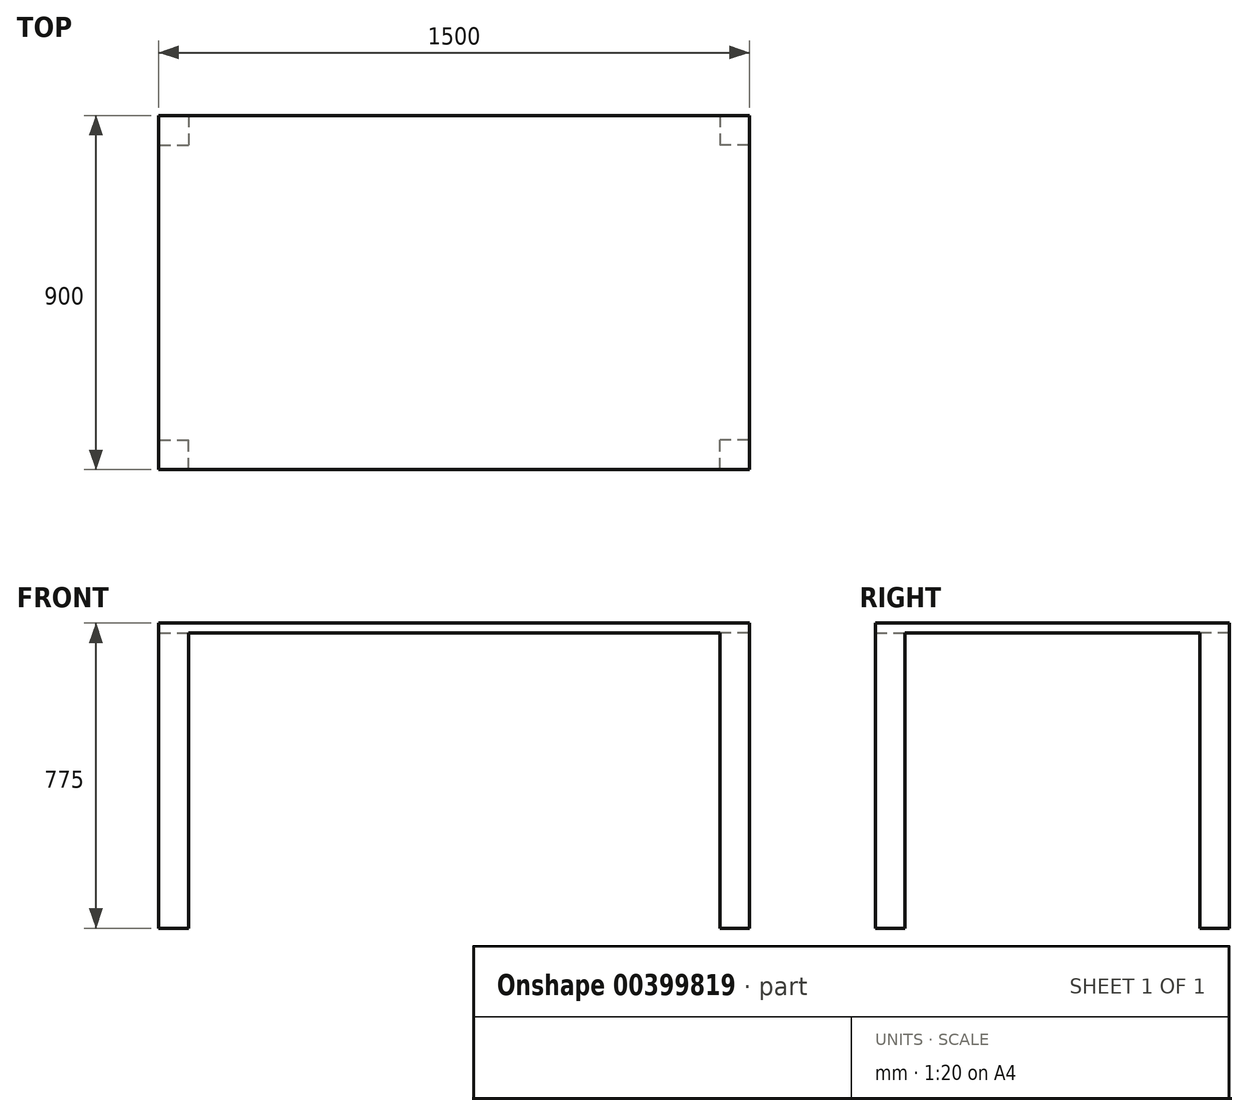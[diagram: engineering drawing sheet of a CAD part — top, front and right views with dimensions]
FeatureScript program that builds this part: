
annotation { "Feature Type Name" : "Feature", "Feature Type Description" : "" }
export const myFeature = defineFeature(function(context is Context, id is Id, definition is map)
    precondition{}
    {
        {
            var Q0;
            Q0=qCreatedBy(makeId("Top.planeOp"),FACE);
            cPlane(context, id + "F0", {"entities" : qUnion([Q0]), "cplaneType" : CPlaneType.OFFSET, "offset" : 750 * mm, "width" : 150 * mm, "height" : 150 * mm});
        }
        {
            var Q0;
            Q0=qCreatedBy(id+"F0.planeOp",FACE);
            var sketch = newSketch(context, id + "F1", { "sketchPlane" : qUnion([Q0])});
            skLineSegment(sketch, "E0.bottom", {"start": v(750, -450) * mm, "end": v(-750, -450) * mm});
            skLineSegment(sketch, "E0.top", {"start": v(750, 450) * mm, "end": v(-750, 450) * mm});
            skLineSegment(sketch, "E0.left", {"start": v(750, -450) * mm, "end": v(750, 450) * mm});
            skLineSegment(sketch, "E0.right", {"start": v(-750, -450) * mm, "end": v(-750, 450) * mm});
            skPoint(sketch, "E0.middle", {"position": v(0, 0) * mm});
            skSolve(sketch);
        }
        {
            var Q0;
            Q0 = qSketchRegion(id + "F1", true);
            extrude(context, id + "F2", {"entities" : qUnion([Q0]), "depth" : 25 * mm});
        }
        {
            var Q0;
            Q0=makeQuery(id+"F2.opExtrude","CAP_FACE",FACE,{"disambiguationData":[OSD([sQuery(id+"F1.wireOp",EDGE,"E0.bottom"),sQuery(id+"F1.wireOp",EDGE,"E0.top"),sQuery(id+"F1.wireOp",EDGE,"E0.left"),sQuery(id+"F1.wireOp",EDGE,"E0.right")])],"isStart":true});
            var sketch = newSketch(context, id + "F3", { "sketchPlane" : qUnion([Q0])});
            skLineSegment(sketch, "E1.bottom", {"start": v(-750, -450) * mm, "end": v(-675, -450) * mm});
            skLineSegment(sketch, "E1.top", {"start": v(-750, -375) * mm, "end": v(-675, -375) * mm});
            skLineSegment(sketch, "E1.left", {"start": v(-750, -450) * mm, "end": v(-750, -375) * mm});
            skLineSegment(sketch, "E1.right", {"start": v(-675, -450) * mm, "end": v(-675, -375) * mm});
            skLineSegment(sketch, "E2.bottom", {"start": v(-750, 450) * mm, "end": v(-675, 450) * mm});
            skLineSegment(sketch, "E2.top", {"start": v(-750, 375) * mm, "end": v(-675, 375) * mm});
            skLineSegment(sketch, "E2.left", {"start": v(-750, 450) * mm, "end": v(-750, 375) * mm});
            skLineSegment(sketch, "E2.right", {"start": v(-675, 450) * mm, "end": v(-675, 375) * mm});
            skLineSegment(sketch, "E3.bottom", {"start": v(750, 450) * mm, "end": v(675, 450) * mm});
            skLineSegment(sketch, "E3.top", {"start": v(750, 375) * mm, "end": v(675, 375) * mm});
            skLineSegment(sketch, "E3.left", {"start": v(750, 450) * mm, "end": v(750, 375) * mm});
            skLineSegment(sketch, "E3.right", {"start": v(675, 450) * mm, "end": v(675, 375) * mm});
            skLineSegment(sketch, "E4.bottom", {"start": v(750, -450) * mm, "end": v(675, -450) * mm});
            skLineSegment(sketch, "E4.top", {"start": v(750, -375) * mm, "end": v(675, -375) * mm});
            skLineSegment(sketch, "E4.left", {"start": v(750, -450) * mm, "end": v(750, -375) * mm});
            skLineSegment(sketch, "E4.right", {"start": v(675, -450) * mm, "end": v(675, -375) * mm});
            skSolve(sketch);
        }
        {
            var Q0;
            Q0 = qSketchRegion(id + "F3", true);
            var Q1;
            Q1=qCreatedBy(makeId("Top.planeOp"),FACE);
            extrude(context, id + "F4", {"entities" : qUnion([Q0]), "operationType" : NewBodyOperationType.ADD, "endBound" : BoundingType.UP_TO_SURFACE, "endBoundEntityFace" : qUnion([Q1]), "depth" : 25 * mm});
        }
    });
